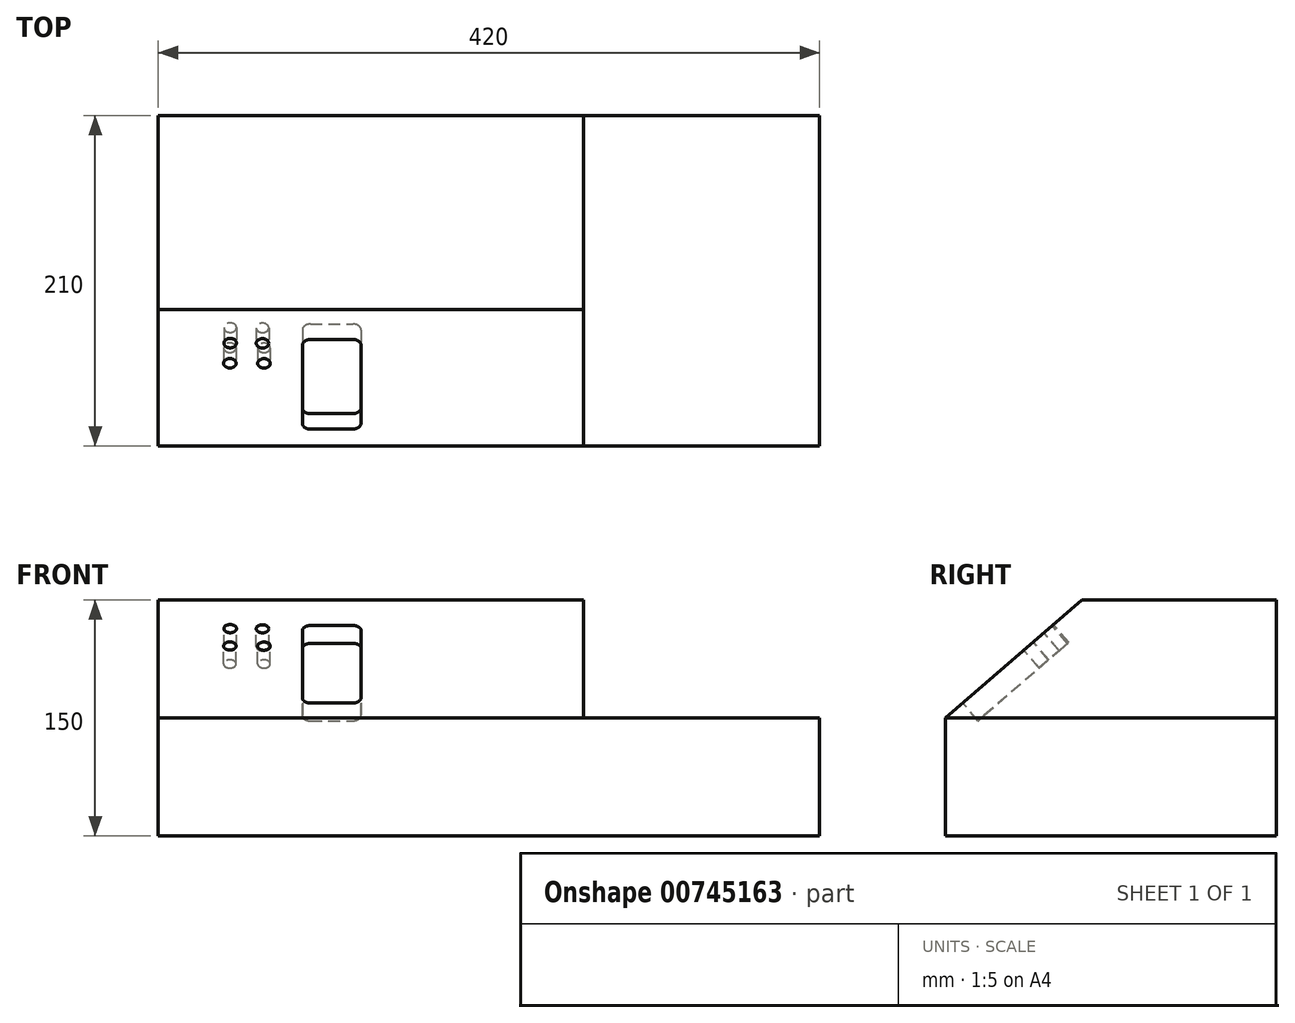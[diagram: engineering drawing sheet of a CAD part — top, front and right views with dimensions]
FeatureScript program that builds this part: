
annotation { "Feature Type Name" : "Feature", "Feature Type Description" : "" }
export const myFeature = defineFeature(function(context is Context, id is Id, definition is map)
    precondition{}
    {
        {
            var Q0;
            Q0=qCreatedBy(makeId("Top.planeOp"),FACE);
            var sketch = newSketch(context, id + "F0", { "sketchPlane" : qUnion([Q0])});
            skLineSegment(sketch, "E0.bottom", {"start": v(0, 0) * mm, "end": v(420, 0) * mm});
            skLineSegment(sketch, "E0.top", {"start": v(0, -210) * mm, "end": v(420, -210) * mm});
            skLineSegment(sketch, "E0.left", {"start": v(0, 0) * mm, "end": v(0, -210) * mm});
            skLineSegment(sketch, "E0.right", {"start": v(420, 0) * mm, "end": v(420, -210) * mm});
            skSolve(sketch);
        }
        {
            var Q0;
            Q0 = qSketchRegion(id + "F0", true);
            extrude(context, id + "F1", {"entities" : qUnion([Q0]), "depth" : 150 * mm, "offsetDistance" : 25 * mm});
        }
        {
            var Q0;
            Q0=makeQuery(id+"F1.opExtrude","SWEPT_FACE",FACE,{"disambiguationData":[OSD([sQuery(id+"F0.wireOp",EDGE,"E0.right")])]});
            var sketch = newSketch(context, id + "F2", { "sketchPlane" : qUnion([Q0])});
            skLineSegment(sketch, "E1", {"start": v(-210, 75) * mm, "end": v(-123.25, 150) * mm});
            skLineSegment(sketch, "E2", {"start": v(-210, 150) * mm, "end": v(-210, 75) * mm});
            skLineSegment(sketch, "E3", {"start": v(-210, 150) * mm, "end": v(-123.25, 150) * mm});
            skSolve(sketch);
        }
        {
            var Q0;
            Q0 = qSketchRegion(id + "F2", true);
            extrude(context, id + "F3", {"entities" : qUnion([Q0]), "operationType" : NewBodyOperationType.REMOVE, "endBound" : BoundingType.THROUGH_ALL, "oppositeDirection" : true, "depth" : 25 * mm, "offsetDistance" : 25 * mm});
        }
        {
            var Q0;
            Q0=makeQuery(id+"F3.boolean.opBoolean","COPY",FACE,{"derivedFrom":makeQuery(id+"F3.opExtrude","SWEPT_FACE",FACE,{"disambiguationData":[OSD([sQuery(id+"F2.wireOp",EDGE,"E1")])]})});
            var sketch = newSketch(context, id + "F4", { "sketchPlane" : qUnion([Q0])});
            skCircle(sketch, "E4", {"center": v(45.67, -23.22) * mm, "radius": 4 * mm});
            skCircle(sketch, "E5", {"center": v(66.24, -23.37) * mm, "radius": 4 * mm});
            skCircle(sketch, "E6", {"center": v(67.18, -40.18) * mm, "radius": 4 * mm});
            skCircle(sketch, "E7", {"center": v(45.5, -40.08) * mm, "radius": 4 * mm});
            skLineSegment(sketch, "E8.bottom", {"start": v(96.62, -20.22) * mm, "end": v(123.86, -20.22) * mm});
            skLineSegment(sketch, "E8.top", {"start": v(96.49, -95.42) * mm, "end": v(123.49, -95.42) * mm});
            skLineSegment(sketch, "E8.left", {"start": v(91.5, -25.33) * mm, "end": v(91.5, -90.44) * mm});
            skLineSegment(sketch, "E8.right", {"start": v(128.86, -25.22) * mm, "end": v(128.86, -90.04) * mm});
            skArc(sketch, "E9", {"start": v(96.62, -20.22) * mm, "mid": v(93, -21.72) * mm, "end": v(91.5, -25.33) * mm});
            skArc(sketch, "E10", {"start": v(128.86, -25.22) * mm, "mid": v(127.4, -21.68) * mm, "end": v(123.86, -20.22) * mm});
            skArc(sketch, "E11", {"start": v(91.5, -90.44) * mm, "mid": v(92.97, -93.96) * mm, "end": v(96.49, -95.42) * mm});
            skArc(sketch, "E12", {"start": v(123.49, -95.42) * mm, "mid": v(127.29, -93.84) * mm, "end": v(128.86, -90.04) * mm});
            skSolve(sketch);
        }
        {
            var Q0;
            Q0 = qSketchRegion(id + "F4", true);
            extrude(context, id + "F5", {"entities" : qUnion([Q0]), "operationType" : NewBodyOperationType.REMOVE, "oppositeDirection" : true, "depth" : 15 * mm, "offsetDistance" : 25 * mm});
        }
        {
            var Q0;
            Q0=makeQuery(id+"F1.opExtrude","SWEPT_FACE",FACE,{"disambiguationData":[OSD([sQuery(id+"F0.wireOp",EDGE,"E0.right")])]});
            var sketch = newSketch(context, id + "F6", { "sketchPlane" : qUnion([Q0])});
            skLineSegment(sketch, "E13", {"start": v(-210, 75) * mm, "end": v(0, 75) * mm});
            skLineSegment(sketch, "E14", {"start": v(0, 75) * mm, "end": v(0, 150) * mm});
            skLineSegment(sketch, "E15", {"start": v(0, 150) * mm, "end": v(-123.25, 150) * mm});
            skLineSegment(sketch, "E16", {"start": v(-123.25, 150) * mm, "end": v(-206.36, 78.14) * mm});
            skSolve(sketch);
        }
        {
            var Q0;
            Q0 = qSketchRegion(id + "F6", true);
            var Q1;
            {var subQ1=sQuery(id+"F6.wireOp",EDGE,"E13");Q1=makeQuery(id+"F6.imprint","IMPRINT",FACE,{"disambiguationData":[TD([[makeQuery(id+"F6.imprint","IMPRINT",EDGE,{"derivedFrom":subQ1}),1.0]])]});}
            extrude(context, id + "F7", {"entities" : qUnion([Q0, Q1]), "operationType" : NewBodyOperationType.REMOVE, "oppositeDirection" : true, "depth" : 150 * mm, "offsetDistance" : 25 * mm});
        }
    });
